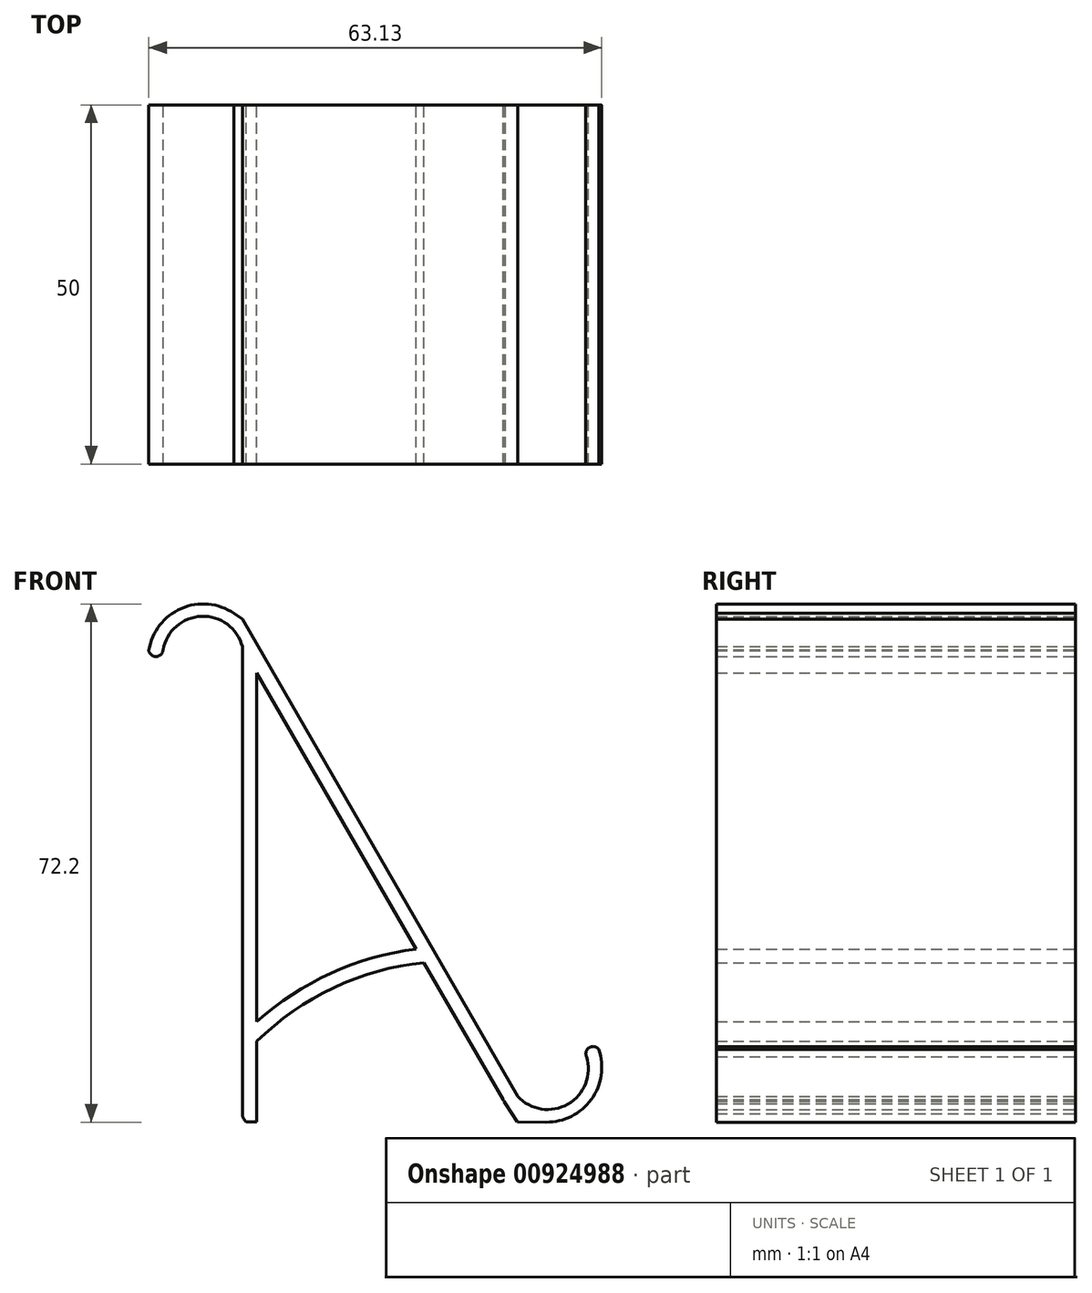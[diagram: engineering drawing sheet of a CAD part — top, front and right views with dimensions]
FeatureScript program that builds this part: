
annotation { "Feature Type Name" : "Feature", "Feature Type Description" : "" }
export const myFeature = defineFeature(function(context is Context, id is Id, definition is map)
    precondition{}
    {
        {
            var Q0;
            Q0=qCreatedBy(makeId("Front.planeOp"),FACE);
            var sketch = newSketch(context, id + "F0", { "sketchPlane" : qUnion([Q0])});
            skLineSegment(sketch, "E0", {"start": v(0, 31.2) * mm, "end": v(0, -33.95) * mm});
            skLineSegment(sketch, "E1", {"start": v(0, 35) * mm, "end": v(38.36, -31.44) * mm});
            skLineSegment(sketch, "E2.0", {"start": v(2, 27.54) * mm, "end": v(28.08, -17.64) * mm});
            skLineSegment(sketch, "E3.trimOffspring", {"start": v(2, 27.54) * mm, "end": v(2, -31.4) * mm});
            skArc(sketch, "E4", {"start": v(36.32, -31.91) * mm, "mid": v(36.38, -32.02) * mm, "end": v(36.44, -32.12) * mm});
            skArc(sketch, "E5", {"start": v(29.22, -19.61) * mm, "mid": v(14.22, -23.4) * mm, "end": v(2.77, -33.8) * mm});
            skArc(sketch, "E6.0", {"start": v(28.08, -17.64) * mm, "mid": v(13.46, -21.54) * mm, "end": v(2, -31.4) * mm});
            skLineSegment(sketch, "E7.trimOffspring", {"start": v(29.22, -19.61) * mm, "end": v(36.32, -31.91) * mm});
            skArc(sketch, "E8", {"start": v(0, -33.84) * mm, "mid": v(0.13, -34.49) * mm, "end": v(0.55, -35) * mm});
            skLineSegment(sketch, "E9", {"start": v(2, -35) * mm, "end": v(2.23, -35) * mm});
            skArc(sketch, "E10.trimOffspring", {"start": v(2.23, -35) * mm, "mid": v(2.65, -34.46) * mm, "end": v(2.77, -33.8) * mm});
            skPoint(sketch, "E11.orphan", {"position": v(0, -35) * mm});
            skLineSegment(sketch, "E12.trimOffspring", {"start": v(0.55, -35) * mm, "end": v(2, -35) * mm});
            skPoint(sketch, "E13.start.orphan", {"position": v(-40.41, -35) * mm});
            skPoint(sketch, "E14.orphan", {"position": v(40.41, -35) * mm});
            skArc(sketch, "E15", {"start": v(41.55, -35) * mm, "mid": v(48.39, -32.19) * mm, "end": v(49.68, -24.9) * mm});
            skLineSegment(sketch, "E16", {"start": v(36.63, -32.44) * mm, "end": v(38.29, -35) * mm});
            skLineSegment(sketch, "E17", {"start": v(38.29, -35) * mm, "end": v(42.32, -35.05) * mm});
            skLineSegment(sketch, "E18.trimOffspring", {"start": v(36.44, -32.12) * mm, "end": v(36.63, -32.44) * mm});
            skPoint(sketch, "E19.MirrorCS.end.orphan", {"position": v(47.94, -25.9) * mm});
            skPoint(sketch, "E19.MirrorCS.start.orphan", {"position": v(9.58, 40.53) * mm});
            skArc(sketch, "E20", {"start": v(38.36, -31.44) * mm, "mid": v(45.38, -32.53) * mm, "end": v(47.94, -25.9) * mm});
            skArc(sketch, "E21", {"start": v(49.68, -24.9) * mm, "mid": v(48.36, -24.64) * mm, "end": v(47.94, -25.9) * mm});
            skLineSegment(sketch, "E22.trimOffspring", {"start": v(47.94, -25.9) * mm, "end": v(49.68, -24.9) * mm});
            skPoint(sketch, "E23.orphan", {"position": v(43.15, -28.68) * mm});
            skPoint(sketch, "E24.startSnap0", {"position": v(15.04, 4.95) * mm});
            skArc(sketch, "E25.MirrorCS", {"start": v(0, 31.2) * mm, "mid": v(-5.7, 35.42) * mm, "end": v(-11.06, 30.75) * mm});
            skArc(sketch, "E26.MirrorCS", {"start": v(-1.17, 35.83) * mm, "mid": v(-8.53, 36.52) * mm, "end": v(-13.05, 30.67) * mm});
            skArc(sketch, "E27.MirrorCS", {"start": v(-13.05, 30.67) * mm, "mid": v(-12.02, 29.82) * mm, "end": v(-11.06, 30.75) * mm});
            skLineSegment(sketch, "E28", {"start": v(-1.17, 35.83) * mm, "end": v(0, 35) * mm});
            skArc(sketch, "E29.0", {"start": v(24.2, -10.93) * mm, "mid": v(12.33, -14.3) * mm, "end": v(2, -21.05) * mm});
            skArc(sketch, "E30.trimOffspring", {"start": v(25.3, -12.82) * mm, "mid": v(12.72, -16.32) * mm, "end": v(2, -23.8) * mm});
            skLineSegment(sketch, "E31", {"start": v(2, -31.4) * mm, "end": v(2, -35) * mm});
            skLineSegment(sketch, "E32", {"start": v(28.08, -17.64) * mm, "end": v(29.22, -19.61) * mm});
            skSolve(sketch);
        }
        {
            var Q0;
            {var subQ0=sQuery(id+"F0.wireOp",EDGE,"E8");var subQ1=sQuery(id+"F0.wireOp",EDGE,"E0");var subQ2=makeQuery(id+"F0.imprint","INTERSECT",VERTEX,{"disambiguationData":[OD(0.0)],"derivedFrom":[subQ1,subQ0]});Q0=makeQuery(id+"F0.imprint","IMPRINT",FACE,{"disambiguationData":[TD([[makeQuery(id+"F0.imprint","IMPRINT",EDGE,{"disambiguationData":[TD([[subQ2,1.0]])],"derivedFrom":subQ1}),-1.0]])]});}
            var Q1;
            Q1=makeQuery(id+"F0.imprint","IMPRINT",FACE,{"disambiguationData":[TD([[makeQuery(id+"F0.imprint","IMPRINT",EDGE,{"derivedFrom":sQuery(id+"F0.wireOp",EDGE,"E21")}),1.0]])]});
            var Q2;
            Q2=makeQuery(id+"F0.imprint","IMPRINT",FACE,{"disambiguationData":[TD([[makeQuery(id+"F0.imprint","IMPRINT",EDGE,{"derivedFrom":sQuery(id+"F0.wireOp",EDGE,"E1")}),-1.0]])]});
            var Q3;
            {var subQ0=sQuery(id+"F0.wireOp",EDGE,"E29.0");Q3=makeQuery(id+"F0.imprint","IMPRINT",FACE,{"disambiguationData":[TD([[makeQuery(id+"F0.imprint","IMPRINT",EDGE,{"derivedFrom":subQ0}),1.0]])]});}
            extrude(context, id + "F1", {"entities" : qUnion([Q0, Q1, Q2, Q3]), "depth" : 50 * mm, "offsetDistance" : 25 * mm});
        }
    });
